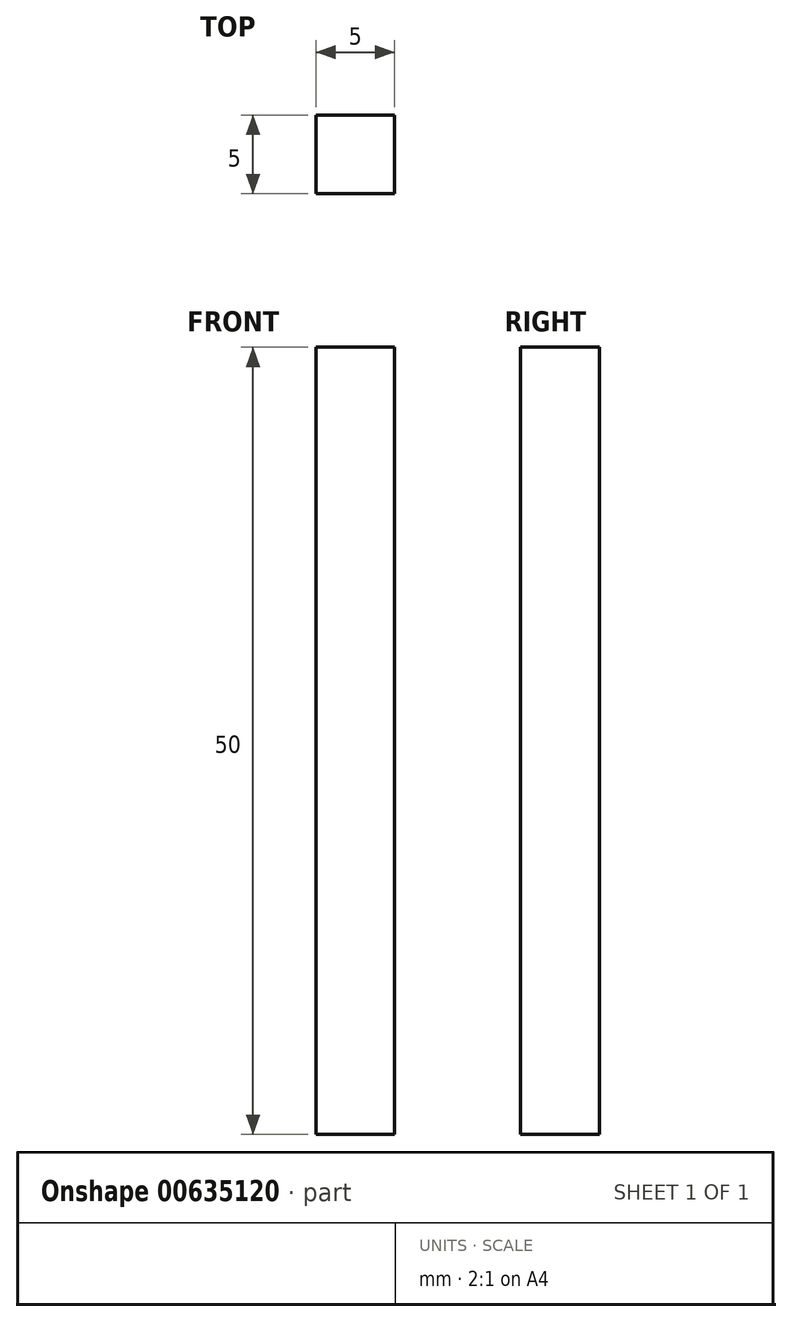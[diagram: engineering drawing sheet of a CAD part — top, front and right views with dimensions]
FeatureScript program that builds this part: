
annotation { "Feature Type Name" : "Feature", "Feature Type Description" : "" }
export const myFeature = defineFeature(function(context is Context, id is Id, definition is map)
    precondition{}
    {
        {
            var Q0;
            Q0=qCreatedBy(makeId("Front.planeOp"),FACE);
            var sketch = newSketch(context, id + "F0", { "sketchPlane" : qUnion([Q0])});
            skLineSegment(sketch, "E0.bottom", {"start": v(-55.56, 31.83) * mm, "end": v(-50.56, 31.83) * mm});
            skLineSegment(sketch, "E0.top", {"start": v(-55.56, -18.17) * mm, "end": v(-50.56, -18.17) * mm});
            skLineSegment(sketch, "E0.left", {"start": v(-55.56, 31.83) * mm, "end": v(-55.56, -18.17) * mm});
            skLineSegment(sketch, "E0.right", {"start": v(-50.56, 31.83) * mm, "end": v(-50.56, -18.17) * mm});
            skSolve(sketch);
        }
        {
            var Q0;
            Q0 = qSketchRegion(id + "F0", true);
            extrude(context, id + "F1", {"entities" : qUnion([Q0]), "depth" : 5 * mm, "offsetDistance" : 25 * mm});
        }
    });
